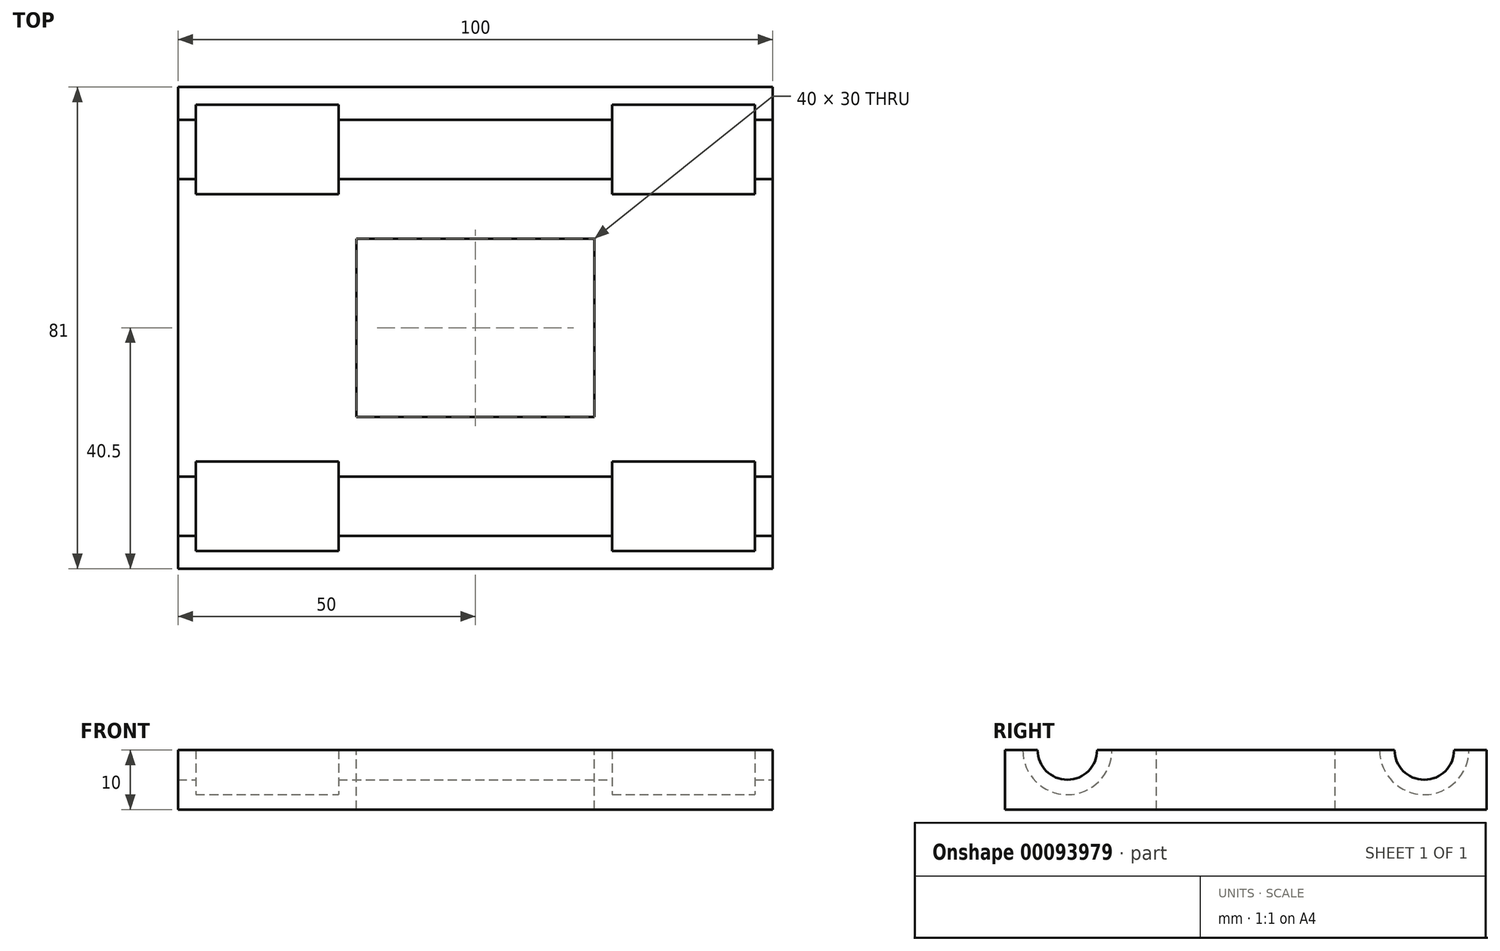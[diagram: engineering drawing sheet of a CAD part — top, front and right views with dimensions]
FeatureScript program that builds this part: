
annotation { "Feature Type Name" : "Feature", "Feature Type Description" : "" }
export const myFeature = defineFeature(function(context is Context, id is Id, definition is map)
    precondition{}
    {
        {
            var Q0;
            Q0=qCreatedBy(makeId("Top.planeOp"),FACE);
            var sketch = newSketch(context, id + "F0", { "sketchPlane" : qUnion([Q0])});
            skLineSegment(sketch, "E0.bottom", {"start": v(20, 15) * mm, "end": v(-20, 15) * mm});
            skLineSegment(sketch, "E0.top", {"start": v(20, -15) * mm, "end": v(-20, -15) * mm});
            skLineSegment(sketch, "E0.left", {"start": v(20, 15) * mm, "end": v(20, -15) * mm});
            skLineSegment(sketch, "E0.right", {"start": v(-20, 15) * mm, "end": v(-20, -15) * mm});
            skPoint(sketch, "E0.middle", {"position": v(0, 0) * mm});
            skLineSegment(sketch, "E1.bottom", {"start": v(50, 40.5) * mm, "end": v(-50, 40.5) * mm});
            skLineSegment(sketch, "E1.top", {"start": v(50, -40.5) * mm, "end": v(-50, -40.5) * mm});
            skLineSegment(sketch, "E1.left", {"start": v(50, 40.5) * mm, "end": v(50, -40.5) * mm});
            skLineSegment(sketch, "E1.right", {"start": v(-50, 40.5) * mm, "end": v(-50, -40.5) * mm});
            skLineSegment(sketch, "E2", {"start": v(-50, 30) * mm, "end": v(50, 30) * mm});
            skLineSegment(sketch, "E3", {"start": v(-50, 35) * mm, "end": v(-47, 35) * mm});
            skLineSegment(sketch, "E4", {"start": v(-47, 35) * mm, "end": v(-47, 37.5) * mm});
            skLineSegment(sketch, "E5", {"start": v(-47, 37.5) * mm, "end": v(-23, 37.5) * mm});
            skLineSegment(sketch, "E6", {"start": v(-23, 37.5) * mm, "end": v(-23, 35) * mm});
            skLineSegment(sketch, "E7", {"start": v(-23, 35) * mm, "end": v(0, 35) * mm});
            skLineSegment(sketch, "E8.MirrorCS", {"start": v(23, 35) * mm, "end": v(0, 35) * mm});
            skLineSegment(sketch, "E9.MirrorCS", {"start": v(23, 37.5) * mm, "end": v(23, 35) * mm});
            skLineSegment(sketch, "E10.MirrorCS", {"start": v(47, 37.5) * mm, "end": v(23, 37.5) * mm});
            skLineSegment(sketch, "E11.MirrorCS", {"start": v(47, 35) * mm, "end": v(47, 37.5) * mm});
            skLineSegment(sketch, "E12.MirrorCS", {"start": v(50, 35) * mm, "end": v(47, 35) * mm});
            skLineSegment(sketch, "E13.MirrorCS", {"start": v(-50, -30) * mm, "end": v(50, -30) * mm});
            skLineSegment(sketch, "E14.MirrorCS", {"start": v(-50, -35) * mm, "end": v(-47, -35) * mm});
            skLineSegment(sketch, "E15.MirrorCS", {"start": v(-47, -35) * mm, "end": v(-47, -37.5) * mm});
            skLineSegment(sketch, "E16.MirrorCS", {"start": v(-47, -37.5) * mm, "end": v(-23, -37.5) * mm});
            skLineSegment(sketch, "E17.MirrorCS", {"start": v(-23, -37.5) * mm, "end": v(-23, -35) * mm});
            skLineSegment(sketch, "E18.MirrorCS", {"start": v(-23, -35) * mm, "end": v(0, -35) * mm});
            skLineSegment(sketch, "E19.MirrorCS", {"start": v(23, -35) * mm, "end": v(0, -35) * mm});
            skLineSegment(sketch, "E20.MirrorCS", {"start": v(23, -37.5) * mm, "end": v(23, -35) * mm});
            skLineSegment(sketch, "E21.MirrorCS", {"start": v(47, -37.5) * mm, "end": v(23, -37.5) * mm});
            skLineSegment(sketch, "E22.MirrorCS", {"start": v(47, -35) * mm, "end": v(47, -37.5) * mm});
            skLineSegment(sketch, "E23.MirrorCS", {"start": v(50, -35) * mm, "end": v(47, -35) * mm});
            skSolve(sketch);
        }
        {
            var Q0;
            {var subQ0=sQuery(id+"F0.wireOp",EDGE,"E13.MirrorCS");Q0=makeQuery(id+"F0.imprint","IMPRINT",FACE,{"disambiguationData":[TD([[makeQuery(id+"F0.imprint","IMPRINT",EDGE,{"derivedFrom":subQ0}),-1.0]])]});}
            var Q1;
            Q1=makeQuery(id+"F0.imprint","IMPRINT",FACE,{"disambiguationData":[TD([[makeQuery(id+"F0.imprint","IMPRINT",EDGE,{"derivedFrom":sQuery(id+"F0.wireOp",EDGE,"E0.bottom")}),-1.0]])]});
            var Q2;
            {var subQ0=sQuery(id+"F0.wireOp",EDGE,"E2");Q2=makeQuery(id+"F0.imprint","IMPRINT",FACE,{"disambiguationData":[TD([[makeQuery(id+"F0.imprint","IMPRINT",EDGE,{"derivedFrom":subQ0}),1.0]])]});}
            var Q3;
            {var subQ0=sQuery(id+"F0.wireOp",EDGE,"E1.top");Q3=makeQuery(id+"F0.imprint","IMPRINT",FACE,{"disambiguationData":[TD([[makeQuery(id+"F0.imprint","IMPRINT",EDGE,{"derivedFrom":subQ0}),-1.0]])]});}
            var Q4;
            {var subQ1=sQuery(id+"F0.wireOp",EDGE,"E1.bottom");Q4=makeQuery(id+"F0.imprint","IMPRINT",FACE,{"disambiguationData":[TD([[makeQuery(id+"F0.imprint","IMPRINT",EDGE,{"derivedFrom":subQ1}),1.0]])]});}
            var Q5;
            Q5=makeQuery(id+"F0.imprint","IMPRINT",FACE,{"disambiguationData":[TD([[makeQuery(id+"F0.imprint","IMPRINT",EDGE,{"derivedFrom":sQuery(id+"F0.wireOp",EDGE,"E0.bottom")}),1.0]])]});
            extrude(context, id + "F1", {"entities" : qUnion([Q0, Q1, Q2, Q3, Q4, Q5]), "oppositeDirection" : true, "depth" : 10 * mm});
        }
        {
            var Q0;
            Q0=makeQuery(id+"F0.imprint","IMPRINT",FACE,{"disambiguationData":[TD([[makeQuery(id+"F0.imprint","IMPRINT",EDGE,{"derivedFrom":sQuery(id+"F0.wireOp",EDGE,"E0.bottom")}),1.0]])]});
            extrude(context, id + "F2", {"entities" : qUnion([Q0]), "operationType" : NewBodyOperationType.REMOVE, "endBound" : BoundingType.THROUGH_ALL, "oppositeDirection" : true, "depth" : 25 * mm});
        }
        {
            var Q0;
            {var subQ0=sQuery(id+"F0.wireOp",EDGE,"E2");Q0=makeQuery(id+"F0.imprint","IMPRINT",FACE,{"disambiguationData":[TD([[makeQuery(id+"F0.imprint","IMPRINT",EDGE,{"derivedFrom":subQ0}),1.0]])]});}
            var Q1;
            Q1=sQuery(id+"F0.wireOp",EDGE,"E2");
            revolve(context, id + "F3", {"operationType" : NewBodyOperationType.REMOVE, "entities" : qUnion([Q0]), "axis" : qUnion([Q1]), "revolveType" : RevolveType.FULL, "oppositeDirection" : true});
        }
        {
            var Q0;
            {var subQ0=sQuery(id+"F0.wireOp",EDGE,"E13.MirrorCS");Q0=makeQuery(id+"F0.imprint","IMPRINT",FACE,{"disambiguationData":[TD([[makeQuery(id+"F0.imprint","IMPRINT",EDGE,{"derivedFrom":subQ0}),-1.0]])]});}
            var Q1;
            Q1=sQuery(id+"F0.wireOp",EDGE,"E13.MirrorCS");
            revolve(context, id + "F4", {"operationType" : NewBodyOperationType.REMOVE, "entities" : qUnion([Q0]), "axis" : qUnion([Q1]), "revolveType" : RevolveType.FULL, "oppositeDirection" : true});
        }
    });
